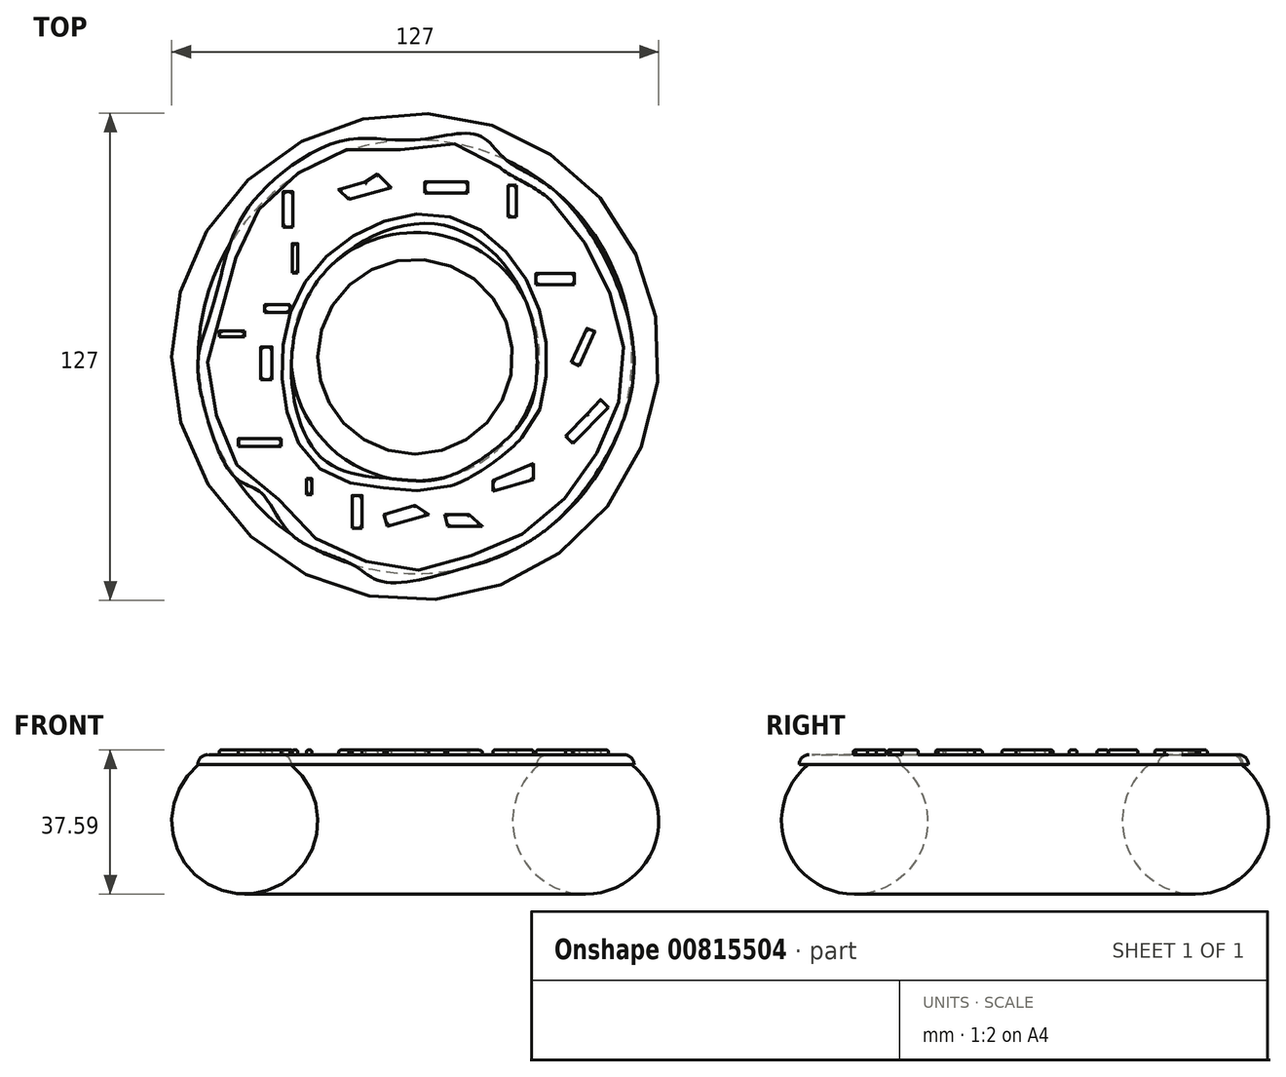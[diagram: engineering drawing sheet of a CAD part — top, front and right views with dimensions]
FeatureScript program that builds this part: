
annotation { "Feature Type Name" : "Feature", "Feature Type Description" : "" }
export const myFeature = defineFeature(function(context is Context, id is Id, definition is map)
    precondition{}
    {
        {
            var Q0;
            Q0=qCreatedBy(makeId("Right.planeOp"),FACE);
            var sketch = newSketch(context, id + "F0", { "sketchPlane" : qUnion([Q0])});
            skPoint(sketch, "E0.0", {"position": v(-44.45, 0) * mm});
            skCircle(sketch, "E1", {"center": v(-44.45, 0) * mm, "radius": 19.05 * mm});
            skLineSegment(sketch, "E2", {"start": v(0, 0) * mm, "end": v(0, 57.85) * mm});
            skSolve(sketch);
        }
        {
            var Q0;
            Q0 = qSketchRegion(id + "F0", true);
            var Q1;
            Q1=sQuery(id+"F0.wireOp",EDGE,"E2");
            revolve(context, id + "F1", {"surfaceOperationType" : NewSurfaceOperationType.NEW, "entities" : qUnion([Q0]), "axis" : qUnion([Q1]), "revolveType" : RevolveType.FULL});
        }
        {
            var Q0;
            Q0=qCreatedBy(makeId("Top.planeOp"),FACE);
            cPlane(context, id + "F2", {"entities" : qUnion([Q0]), "cplaneType" : CPlaneType.OFFSET, "offset" : 25.4 * mm, "width" : 152.4 * mm, "height" : 152.4 * mm});
        }
        {
            var Q0;
            Q0=qCreatedBy(id+"F2.planeOp",FACE);
            var sketch = newSketch(context, id + "F3", { "sketchPlane" : qUnion([Q0])});
            skLineSegment(sketch, "E3.bottom", {"start": v(71.75, 72.74) * mm, "end": v(-67.97, 72.74) * mm});
            skLineSegment(sketch, "E3.top", {"start": v(71.75, -72.74) * mm, "end": v(-67.97, -72.74) * mm});
            skLineSegment(sketch, "E3.left", {"start": v(71.75, 72.74) * mm, "end": v(71.75, -72.74) * mm});
            skLineSegment(sketch, "E3.right", {"start": v(-67.97, 72.74) * mm, "end": v(-67.97, -72.74) * mm});
            skPoint(sketch, "E3.middle", {"position": v(1.89, 0) * mm});
            skSolve(sketch);
        }
        {
            var Q0;
            Q0 = qSketchRegion(id + "F3", true);
            extrude(context, id + "F4", {"entities" : qUnion([Q0]), "operationType" : NewBodyOperationType.REMOVE, "oppositeDirection" : true, "depth" : 10.67 * mm, "offsetDistance" : 25.4 * mm});
        }
        {
            var Q0;
            Q0=makeQuery(id+"F4.boolean.opBoolean","COPY",FACE,{"derivedFrom":makeQuery(id+"F4.opExtrude","CAP_FACE",FACE,{"disambiguationData":[OSD([sQuery(id+"F3.wireOp",EDGE,"E3.bottom"),sQuery(id+"F3.wireOp",EDGE,"E3.top"),sQuery(id+"F3.wireOp",EDGE,"E3.left"),sQuery(id+"F3.wireOp",EDGE,"E3.right")])],"isStart":false})});
            var sketch = newSketch(context, id + "F5", { "sketchPlane" : qUnion([Q0])});
            skFitSpline(sketch, "E4", {"points": [v(23.69, 51.33) * mm, v(16.27, 57.85) * mm, v(0, 56.53) * mm, v(-19.2, 56.27) * mm, v(-40.05, 43.01) * mm, v(-48.28, 29.4) * mm, v(-52.95, 12.49) * mm, v(-56.53, 0) * mm, v(-54.73, -14.13) * mm, v(-47, -31.4) * mm, v(-39.96, -35.68) * mm, v(-32.08, -46.55) * mm, v(-16.56, -54.05) * mm, v(-8.73, -58.59) * mm, v(13, -55.01) * mm, v(34.64, -44.67) * mm, v(53, -19.65) * mm, v(55.82, 8.92) * mm, v(36.95, 42.78) * mm, v(23.69, 51.33) * mm]});
            skFitSpline(sketch, "E5", {"points": [v(25.95, -19.35) * mm, v(8.41, -31.26) * mm, v(-5.92, -31.83) * mm, v(-23.93, -26.74) * mm, v(-32.28, -2.5) * mm, v(-22.24, 23.52) * mm, v(6.85, 34.4) * mm, v(28.6, 15.18) * mm, v(31.17, -8.74) * mm, v(25.95, -19.35) * mm]});
            skSolve(sketch);
        }
        {
            var Q0;
            Q0 = qSketchRegion(id + "F5", true);
            extrude(context, id + "F6", {"entities" : qUnion([Q0]), "operationType" : NewBodyOperationType.ADD, "depth" : 2.54 * mm, "offsetDistance" : 25.4 * mm});
        }
        {
            var Q0;
            Q0=makeQuery(id+"F6.opExtrude","CAP_FACE",FACE,{"disambiguationData":[OSD([sQuery(id+"F5.wireOp",EDGE,"E4"),sQuery(id+"F5.wireOp",EDGE,"E5")])],"isStart":false});
            fillet(context, id + "F7", {"entities" : qUnion([Q0]), "radius" : 2.54 * mm, "tangentPropagation" : true, "allowEdgeOverflow" : false});
        }
        {
            var Q0;
            Q0=makeQuery(id+"F6.opExtrude","CAP_FACE",FACE,{"disambiguationData":[OSD([sQuery(id+"F5.wireOp",EDGE,"E4"),sQuery(id+"F5.wireOp",EDGE,"E5")])],"isStart":false});
            var sketch = newSketch(context, id + "F8", { "sketchPlane" : qUnion([Q0])});
            skLineSegment(sketch, "E6.bottom", {"start": v(13.73, 45.55) * mm, "end": v(2.48, 45.55) * mm});
            skLineSegment(sketch, "E6.top", {"start": v(13.73, 42.65) * mm, "end": v(2.48, 42.65) * mm});
            skLineSegment(sketch, "E6.left", {"start": v(13.73, 45.55) * mm, "end": v(13.73, 42.65) * mm});
            skLineSegment(sketch, "E6.right", {"start": v(2.48, 45.55) * mm, "end": v(2.48, 42.65) * mm});
            skPoint(sketch, "E6.middle", {"position": v(8.1, 44.1) * mm});
            skLineSegment(sketch, "E7.bottom", {"start": v(26.4, 36.42) * mm, "end": v(24.24, 36.42) * mm});
            skLineSegment(sketch, "E7.top", {"start": v(26.4, 44.68) * mm, "end": v(24.24, 44.68) * mm});
            skLineSegment(sketch, "E7.left", {"start": v(26.4, 36.42) * mm, "end": v(26.4, 44.68) * mm});
            skLineSegment(sketch, "E7.right", {"start": v(24.24, 36.42) * mm, "end": v(24.24, 44.68) * mm});
            skPoint(sketch, "E7.middle", {"position": v(25.32, 40.55) * mm});
            skLineSegment(sketch, "E8.bottom", {"start": v(41.53, 18.81) * mm, "end": v(31.5, 18.81) * mm});
            skLineSegment(sketch, "E8.top", {"start": v(41.53, 21.73) * mm, "end": v(31.5, 21.73) * mm});
            skLineSegment(sketch, "E8.left", {"start": v(41.53, 18.81) * mm, "end": v(41.53, 21.73) * mm});
            skLineSegment(sketch, "E8.right", {"start": v(31.5, 18.81) * mm, "end": v(31.5, 21.73) * mm});
            skPoint(sketch, "E8.middle", {"position": v(36.52, 20.27) * mm});
            skLineSegment(sketch, "E9", {"start": v(44.74, 7.4) * mm, "end": v(40.72, -1.43) * mm});
            skLineSegment(sketch, "E10", {"start": v(40.72, -1.43) * mm, "end": v(42.76, -2.36) * mm});
            skLineSegment(sketch, "E11", {"start": v(42.76, -2.36) * mm, "end": v(46.85, 6.62) * mm});
            skLineSegment(sketch, "E12", {"start": v(46.85, 6.62) * mm, "end": v(44.74, 7.4) * mm});
            skLineSegment(sketch, "E13", {"start": v(44.74, -15.04) * mm, "end": v(39.2, -20.68) * mm});
            skLineSegment(sketch, "E14", {"start": v(39.2, -20.68) * mm, "end": v(41.16, -22.6) * mm});
            skLineSegment(sketch, "E15", {"start": v(41.16, -22.6) * mm, "end": v(50.43, -13.15) * mm});
            skLineSegment(sketch, "E16", {"start": v(50.43, -13.15) * mm, "end": v(48.35, -11.11) * mm});
            skLineSegment(sketch, "E17", {"start": v(48.35, -11.11) * mm, "end": v(44.74, -15.04) * mm});
            skLineSegment(sketch, "E18", {"start": v(30.82, -27.8) * mm, "end": v(30.82, -32.04) * mm});
            skLineSegment(sketch, "E19", {"start": v(30.82, -32.04) * mm, "end": v(20.26, -35.03) * mm});
            skLineSegment(sketch, "E20", {"start": v(20.26, -35.03) * mm, "end": v(20.26, -32.3) * mm});
            skLineSegment(sketch, "E21", {"start": v(20.26, -32.3) * mm, "end": v(30.82, -27.8) * mm});
            skLineSegment(sketch, "E22", {"start": v(14.04, -41.1) * mm, "end": v(7.66, -41.1) * mm});
            skLineSegment(sketch, "E23", {"start": v(7.66, -41.1) * mm, "end": v(8.52, -44.14) * mm});
            skLineSegment(sketch, "E24", {"start": v(8.52, -44.14) * mm, "end": v(17.48, -44.14) * mm});
            skLineSegment(sketch, "E25", {"start": v(17.48, -44.14) * mm, "end": v(14.04, -41.1) * mm});
            skLineSegment(sketch, "E26", {"start": v(0, -38.8) * mm, "end": v(-8.13, -41.1) * mm});
            skLineSegment(sketch, "E27", {"start": v(-8.13, -41.1) * mm, "end": v(-7.27, -44.14) * mm});
            skLineSegment(sketch, "E28", {"start": v(-7.27, -44.14) * mm, "end": v(3.47, -41.1) * mm});
            skLineSegment(sketch, "E29", {"start": v(3.47, -41.1) * mm, "end": v(0, -38.8) * mm});
            skLineSegment(sketch, "E30", {"start": v(-13, 45.55) * mm, "end": v(-20, 43.57) * mm});
            skLineSegment(sketch, "E31", {"start": v(-20, 43.57) * mm, "end": v(-17.34, 40.97) * mm});
            skLineSegment(sketch, "E32", {"start": v(-17.34, 40.97) * mm, "end": v(-6.28, 44.1) * mm});
            skLineSegment(sketch, "E33", {"start": v(-6.28, 44.1) * mm, "end": v(-9.82, 47.57) * mm});
            skLineSegment(sketch, "E34", {"start": v(-9.82, 47.57) * mm, "end": v(-13, 45.55) * mm});
            skLineSegment(sketch, "E35.bottom", {"start": v(-34.45, 33.82) * mm, "end": v(-31.95, 33.82) * mm});
            skLineSegment(sketch, "E35.top", {"start": v(-34.45, 43.08) * mm, "end": v(-31.95, 43.08) * mm});
            skLineSegment(sketch, "E35.left", {"start": v(-34.45, 33.82) * mm, "end": v(-34.45, 43.08) * mm});
            skLineSegment(sketch, "E35.right", {"start": v(-31.95, 33.82) * mm, "end": v(-31.95, 43.08) * mm});
            skPoint(sketch, "E35.middle", {"position": v(-33.2, 38.45) * mm});
            skLineSegment(sketch, "E36.bottom", {"start": v(-32.07, 21.8) * mm, "end": v(-30.63, 21.8) * mm});
            skLineSegment(sketch, "E36.top", {"start": v(-32.07, 29.5) * mm, "end": v(-30.63, 29.5) * mm});
            skLineSegment(sketch, "E36.left", {"start": v(-32.07, 21.8) * mm, "end": v(-32.07, 29.5) * mm});
            skLineSegment(sketch, "E36.right", {"start": v(-30.63, 21.8) * mm, "end": v(-30.63, 29.5) * mm});
            skPoint(sketch, "E36.middle", {"position": v(-31.35, 25.65) * mm});
            skLineSegment(sketch, "E37.bottom", {"start": v(-39.23, 13.56) * mm, "end": v(-32.7, 13.56) * mm});
            skLineSegment(sketch, "E37.top", {"start": v(-39.23, 11.54) * mm, "end": v(-32.7, 11.54) * mm});
            skLineSegment(sketch, "E37.left", {"start": v(-39.23, 13.56) * mm, "end": v(-39.23, 11.54) * mm});
            skLineSegment(sketch, "E37.right", {"start": v(-32.7, 13.56) * mm, "end": v(-32.7, 11.54) * mm});
            skPoint(sketch, "E37.middle", {"position": v(-35.96, 12.55) * mm});
            skLineSegment(sketch, "E38.bottom", {"start": v(-44.47, 6.78) * mm, "end": v(-51.08, 6.78) * mm});
            skLineSegment(sketch, "E38.top", {"start": v(-44.47, 5.22) * mm, "end": v(-51.08, 5.22) * mm});
            skLineSegment(sketch, "E38.left", {"start": v(-44.47, 6.78) * mm, "end": v(-44.47, 5.22) * mm});
            skLineSegment(sketch, "E38.right", {"start": v(-51.08, 6.78) * mm, "end": v(-51.08, 5.22) * mm});
            skPoint(sketch, "E38.middle", {"position": v(-47.77, 6) * mm});
            skLineSegment(sketch, "E39.bottom", {"start": v(-40.27, -5.98) * mm, "end": v(-37.33, -5.98) * mm});
            skLineSegment(sketch, "E39.top", {"start": v(-40.27, 2.55) * mm, "end": v(-37.33, 2.55) * mm});
            skLineSegment(sketch, "E39.left", {"start": v(-40.27, -5.98) * mm, "end": v(-40.27, 2.55) * mm});
            skLineSegment(sketch, "E39.right", {"start": v(-37.33, -5.98) * mm, "end": v(-37.33, 2.55) * mm});
            skPoint(sketch, "E39.middle", {"position": v(-38.8, -1.72) * mm});
            skLineSegment(sketch, "E40.bottom", {"start": v(-34.96, -23.32) * mm, "end": v(-46.2, -23.32) * mm});
            skLineSegment(sketch, "E40.top", {"start": v(-34.96, -21.4) * mm, "end": v(-46.2, -21.4) * mm});
            skLineSegment(sketch, "E40.left", {"start": v(-34.96, -23.32) * mm, "end": v(-34.96, -21.4) * mm});
            skLineSegment(sketch, "E40.right", {"start": v(-46.2, -23.32) * mm, "end": v(-46.2, -21.4) * mm});
            skPoint(sketch, "E40.middle", {"position": v(-40.58, -22.36) * mm});
            skLineSegment(sketch, "E41.bottom", {"start": v(-26.92, -35.88) * mm, "end": v(-28.33, -35.88) * mm});
            skLineSegment(sketch, "E41.top", {"start": v(-26.92, -31.77) * mm, "end": v(-28.33, -31.77) * mm});
            skLineSegment(sketch, "E41.left", {"start": v(-26.92, -35.88) * mm, "end": v(-26.92, -31.77) * mm});
            skLineSegment(sketch, "E41.right", {"start": v(-28.33, -35.88) * mm, "end": v(-28.33, -31.77) * mm});
            skPoint(sketch, "E41.middle", {"position": v(-27.63, -33.82) * mm});
            skLineSegment(sketch, "E42.bottom", {"start": v(-13.82, -44.72) * mm, "end": v(-16.44, -44.72) * mm});
            skLineSegment(sketch, "E42.top", {"start": v(-13.82, -36.18) * mm, "end": v(-16.44, -36.18) * mm});
            skLineSegment(sketch, "E42.left", {"start": v(-13.82, -44.72) * mm, "end": v(-13.82, -36.18) * mm});
            skLineSegment(sketch, "E42.right", {"start": v(-16.44, -44.72) * mm, "end": v(-16.44, -36.18) * mm});
            skPoint(sketch, "E42.middle", {"position": v(-15.13, -40.45) * mm});
            skSolve(sketch);
        }
        {
            var Q0;
            Q0 = qSketchRegion(id + "F8", true);
            extrude(context, id + "F9", {"entities" : qUnion([Q0]), "operationType" : NewBodyOperationType.ADD, "depth" : 1.27 * mm, "offsetDistance" : 25.4 * mm});
        }
        {
            var Q0;
            Q0=makeQuery(id+"F9.opExtrude","CAP_FACE",FACE,{"disambiguationData":[OSD([sQuery(id+"F8.wireOp",EDGE,"E35.bottom"),sQuery(id+"F8.wireOp",EDGE,"E35.top"),sQuery(id+"F8.wireOp",EDGE,"E35.left"),sQuery(id+"F8.wireOp",EDGE,"E35.right")])],"isStart":false});
            var Q1;
            Q1=makeQuery(id+"F9.opExtrude","CAP_FACE",FACE,{"disambiguationData":[OSD([sQuery(id+"F8.wireOp",EDGE,"E36.bottom"),sQuery(id+"F8.wireOp",EDGE,"E36.top"),sQuery(id+"F8.wireOp",EDGE,"E36.left"),sQuery(id+"F8.wireOp",EDGE,"E36.right")])],"isStart":false});
            var Q2;
            Q2=makeQuery(id+"F9.opExtrude","CAP_FACE",FACE,{"disambiguationData":[OSD([sQuery(id+"F8.wireOp",EDGE,"E37.bottom"),sQuery(id+"F8.wireOp",EDGE,"E37.top"),sQuery(id+"F8.wireOp",EDGE,"E37.left"),sQuery(id+"F8.wireOp",EDGE,"E37.right")])],"isStart":false});
            var Q3;
            Q3=makeQuery(id+"F9.opExtrude","CAP_FACE",FACE,{"disambiguationData":[OSD([sQuery(id+"F8.wireOp",EDGE,"E38.bottom"),sQuery(id+"F8.wireOp",EDGE,"E38.top"),sQuery(id+"F8.wireOp",EDGE,"E38.left"),sQuery(id+"F8.wireOp",EDGE,"E38.right")])],"isStart":false});
            var Q4;
            Q4=makeQuery(id+"F9.opExtrude","CAP_FACE",FACE,{"disambiguationData":[OSD([sQuery(id+"F8.wireOp",EDGE,"E39.bottom"),sQuery(id+"F8.wireOp",EDGE,"E39.top"),sQuery(id+"F8.wireOp",EDGE,"E39.left"),sQuery(id+"F8.wireOp",EDGE,"E39.right")])],"isStart":false});
            var Q5;
            Q5=makeQuery(id+"F9.opExtrude","CAP_FACE",FACE,{"disambiguationData":[OSD([sQuery(id+"F8.wireOp",EDGE,"E30"),sQuery(id+"F8.wireOp",EDGE,"E31"),sQuery(id+"F8.wireOp",EDGE,"E32"),sQuery(id+"F8.wireOp",EDGE,"E33"),sQuery(id+"F8.wireOp",EDGE,"E34")])],"isStart":false});
            var Q6;
            Q6=makeQuery(id+"F9.opExtrude","CAP_FACE",FACE,{"disambiguationData":[OSD([sQuery(id+"F8.wireOp",EDGE,"E6.bottom"),sQuery(id+"F8.wireOp",EDGE,"E6.top"),sQuery(id+"F8.wireOp",EDGE,"E6.left"),sQuery(id+"F8.wireOp",EDGE,"E6.right")])],"isStart":false});
            var Q7;
            Q7=makeQuery(id+"F9.opExtrude","CAP_FACE",FACE,{"disambiguationData":[OSD([sQuery(id+"F8.wireOp",EDGE,"E7.bottom"),sQuery(id+"F8.wireOp",EDGE,"E7.top"),sQuery(id+"F8.wireOp",EDGE,"E7.left"),sQuery(id+"F8.wireOp",EDGE,"E7.right")])],"isStart":false});
            var Q8;
            Q8=makeQuery(id+"F9.opExtrude","CAP_FACE",FACE,{"disambiguationData":[OSD([sQuery(id+"F8.wireOp",EDGE,"E8.bottom"),sQuery(id+"F8.wireOp",EDGE,"E8.top"),sQuery(id+"F8.wireOp",EDGE,"E8.left"),sQuery(id+"F8.wireOp",EDGE,"E8.right")])],"isStart":false});
            var Q9;
            Q9=makeQuery(id+"F9.opExtrude","CAP_FACE",FACE,{"disambiguationData":[OSD([sQuery(id+"F8.wireOp",EDGE,"E9"),sQuery(id+"F8.wireOp",EDGE,"E10"),sQuery(id+"F8.wireOp",EDGE,"E11"),sQuery(id+"F8.wireOp",EDGE,"E12")])],"isStart":false});
            var Q10;
            Q10=makeQuery(id+"F9.opExtrude","CAP_FACE",FACE,{"disambiguationData":[OSD([sQuery(id+"F8.wireOp",EDGE,"E13"),sQuery(id+"F8.wireOp",EDGE,"E14"),sQuery(id+"F8.wireOp",EDGE,"E15"),sQuery(id+"F8.wireOp",EDGE,"E16"),sQuery(id+"F8.wireOp",EDGE,"E17")])],"isStart":false});
            var Q11;
            Q11=makeQuery(id+"F9.opExtrude","CAP_FACE",FACE,{"disambiguationData":[OSD([sQuery(id+"F8.wireOp",EDGE,"E18"),sQuery(id+"F8.wireOp",EDGE,"E19"),sQuery(id+"F8.wireOp",EDGE,"E20"),sQuery(id+"F8.wireOp",EDGE,"E21")])],"isStart":false});
            var Q12;
            Q12=makeQuery(id+"F9.opExtrude","CAP_FACE",FACE,{"disambiguationData":[OSD([sQuery(id+"F8.wireOp",EDGE,"E22"),sQuery(id+"F8.wireOp",EDGE,"E23"),sQuery(id+"F8.wireOp",EDGE,"E24"),sQuery(id+"F8.wireOp",EDGE,"E25")])],"isStart":false});
            var Q13;
            Q13=makeQuery(id+"F9.opExtrude","CAP_FACE",FACE,{"disambiguationData":[OSD([sQuery(id+"F8.wireOp",EDGE,"E26"),sQuery(id+"F8.wireOp",EDGE,"E27"),sQuery(id+"F8.wireOp",EDGE,"E28"),sQuery(id+"F8.wireOp",EDGE,"E29")])],"isStart":false});
            var Q14;
            Q14=makeQuery(id+"F9.opExtrude","CAP_FACE",FACE,{"disambiguationData":[OSD([sQuery(id+"F8.wireOp",EDGE,"E42.bottom"),sQuery(id+"F8.wireOp",EDGE,"E42.top"),sQuery(id+"F8.wireOp",EDGE,"E42.left"),sQuery(id+"F8.wireOp",EDGE,"E42.right")])],"isStart":false});
            var Q15;
            Q15=makeQuery(id+"F9.opExtrude","CAP_FACE",FACE,{"disambiguationData":[OSD([sQuery(id+"F8.wireOp",EDGE,"E40.bottom"),sQuery(id+"F8.wireOp",EDGE,"E40.top"),sQuery(id+"F8.wireOp",EDGE,"E40.left"),sQuery(id+"F8.wireOp",EDGE,"E40.right")])],"isStart":false});
            var Q16;
            Q16=makeQuery(id+"F9.opExtrude","CAP_FACE",FACE,{"disambiguationData":[OSD([sQuery(id+"F8.wireOp",EDGE,"E41.bottom"),sQuery(id+"F8.wireOp",EDGE,"E41.top"),sQuery(id+"F8.wireOp",EDGE,"E41.left"),sQuery(id+"F8.wireOp",EDGE,"E41.right")])],"isStart":false});
            fillet(context, id + "F10", {"entities" : qUnion([Q0, Q1, Q2, Q3, Q4, Q5, Q6, Q7, Q8, Q9, Q10, Q11, Q12, Q13, Q14, Q15, Q16]), "radius" : 0.5 * mm, "tangentPropagation" : true, "allowEdgeOverflow" : false});
        }
    });
